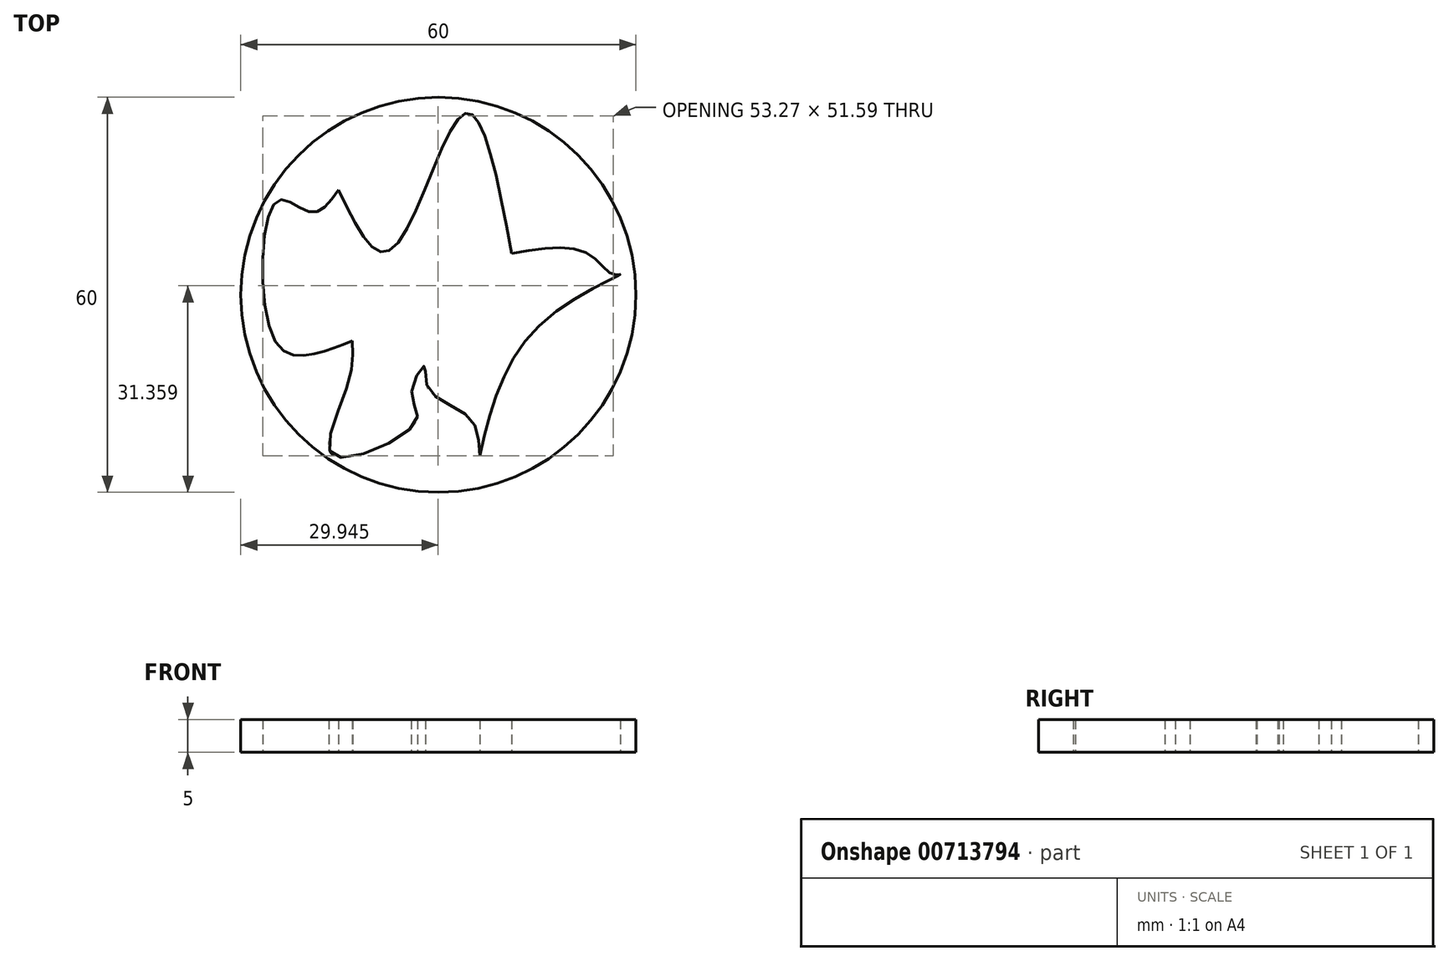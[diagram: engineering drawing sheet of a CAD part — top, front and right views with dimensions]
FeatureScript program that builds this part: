
annotation { "Feature Type Name" : "Feature", "Feature Type Description" : "" }
export const myFeature = defineFeature(function(context is Context, id is Id, definition is map)
    precondition{}
    {
        {
            var Q0;
            Q0=qCreatedBy(makeId("Top.planeOp"),FACE);
            var sketch = newSketch(context, id + "F0", { "sketchPlane" : qUnion([Q0])});
            skCircle(sketch, "E0", {"center": v(0, 0) * mm, "radius": 30 * mm});
            skFitSpline(sketch, "E1", {"points": [v(6.27, -24.44) * mm, v(4.54, -18.46) * mm, v(-1.6, -14.15) * mm, v(-2.1, -10.84) * mm, v(-4.09, -14.98) * mm, v(-3.42, -19.3) * mm, v(-15.86, -24.44) * mm, v(-13.87, -13.99) * mm, v(-13.04, -7.02) * mm], "startDerivative": vector(-2.23, 56.43) * mm, "endDerivative": vector(-1.96, 46.2) * mm});
            skFitSpline(sketch, "E2", {"points": [v(-13.04, -7.02) * mm, v(-18.9, -8.97) * mm, v(-24.78, -7.02) * mm, v(-24.47, 14.24) * mm, v(-19.36, 12.54) * mm, v(-15.18, 15.94) * mm], "startDerivative": vector(-32.27, -12.73) * mm, "endDerivative": vector(23.2, 33.67) * mm});
            skFitSpline(sketch, "E3", {"points": [v(-15.18, 15.94) * mm, v(-7.28, 6.8) * mm, v(3.7, 27.4) * mm, v(11.14, 6.3) * mm], "startDerivative": vector(29.1, -61.04) * mm, "endDerivative": vector(18.04, -95.48) * mm});
            skFitSpline(sketch, "E4", {"points": [v(11.14, 6.3) * mm, v(22.62, 6.3) * mm, v(26.5, 3.09) * mm, v(27.63, 3.09) * mm, v(15.68, -4.34) * mm, v(6.27, -24.44) * mm], "startDerivative": vector(59.28, 9.74) * mm, "endDerivative": vector(-17.07, -71.05) * mm});
            skSolve(sketch);
        }
        {
            var Q0;
            Q0=qSketchRegion(id+"F0",true);
            extrude(context, id + "F1", {"entities" : qUnion([Q0]), "depth" : 5 * mm, "offsetDistance" : 25 * mm});
        }
    });
